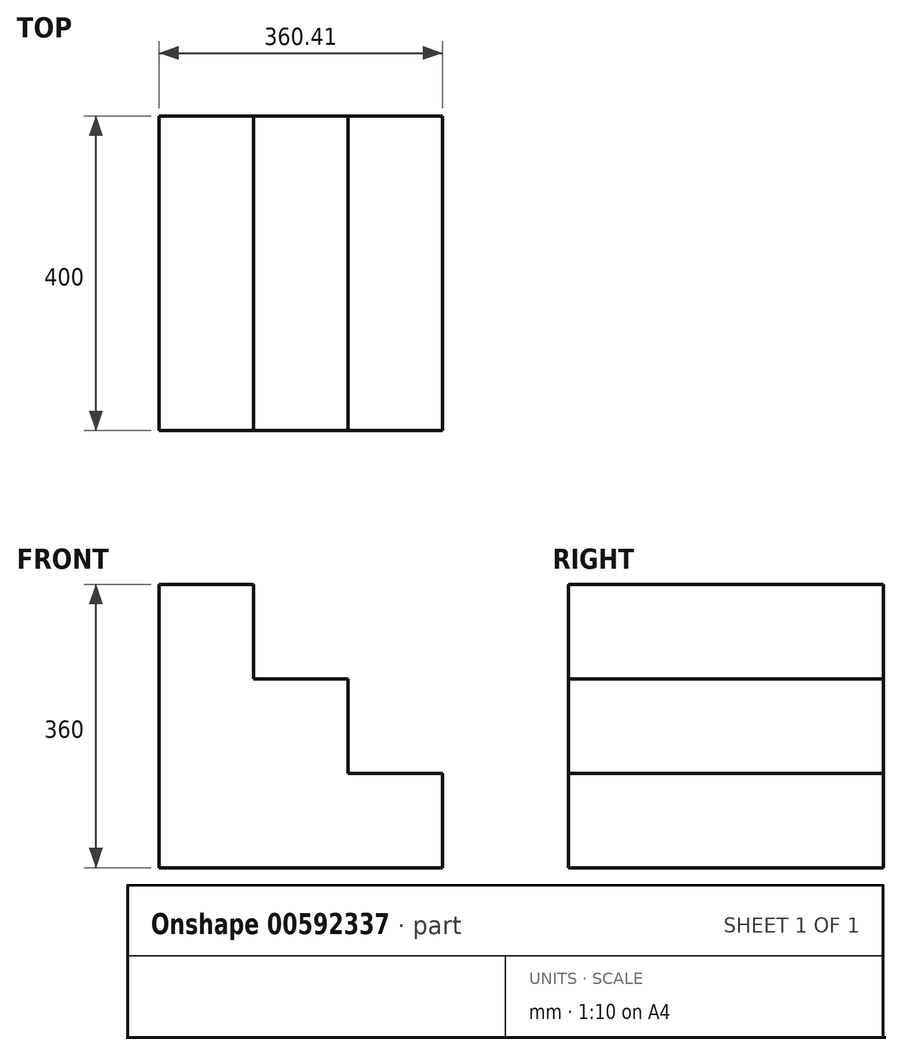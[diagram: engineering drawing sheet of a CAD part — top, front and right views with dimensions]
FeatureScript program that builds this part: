
annotation { "Feature Type Name" : "Feature", "Feature Type Description" : "" }
export const myFeature = defineFeature(function(context is Context, id is Id, definition is map)
    precondition{}
    {
        {
            var Q0;
            Q0=qCreatedBy(makeId("Front.planeOp"),FACE);
            var sketch = newSketch(context, id + "F0", { "sketchPlane" : qUnion([Q0])});
            skLineSegment(sketch, "E0", {"start": v(0, 0) * mm, "end": v(360, 0) * mm});
            skLineSegment(sketch, "E1", {"start": v(0, 0) * mm, "end": v(0, 360) * mm});
            skLineSegment(sketch, "E2", {"start": v(0, 360) * mm, "end": v(120, 360) * mm});
            skLineSegment(sketch, "E3", {"start": v(120, 360) * mm, "end": v(120, 239.98) * mm});
            skLineSegment(sketch, "E4", {"start": v(120, 239.98) * mm, "end": v(240.2, 239.98) * mm});
            skLineSegment(sketch, "E5", {"start": v(240.2, 239.98) * mm, "end": v(240.2, 119.77) * mm});
            skLineSegment(sketch, "E6", {"start": v(240.2, 119.77) * mm, "end": v(360.4, 119.77) * mm});
            skLineSegment(sketch, "E7", {"start": v(360.4, 119.77) * mm, "end": v(360, 0) * mm});
            skSolve(sketch);
        }
        {
            var Q0;
            Q0=makeQuery(id+"F0.imprint","IMPRINT",FACE,{"disambiguationData":[TD([[makeQuery(id+"F0.imprint","IMPRINT",EDGE,{"derivedFrom":sQuery(id+"F0.wireOp",EDGE,"E0")}),1.0]])]});
            extrude(context, id + "F1", {"entities" : qUnion([Q0]), "depth" : 400 * mm, "offsetDistance" : 25 * mm});
        }
    });
